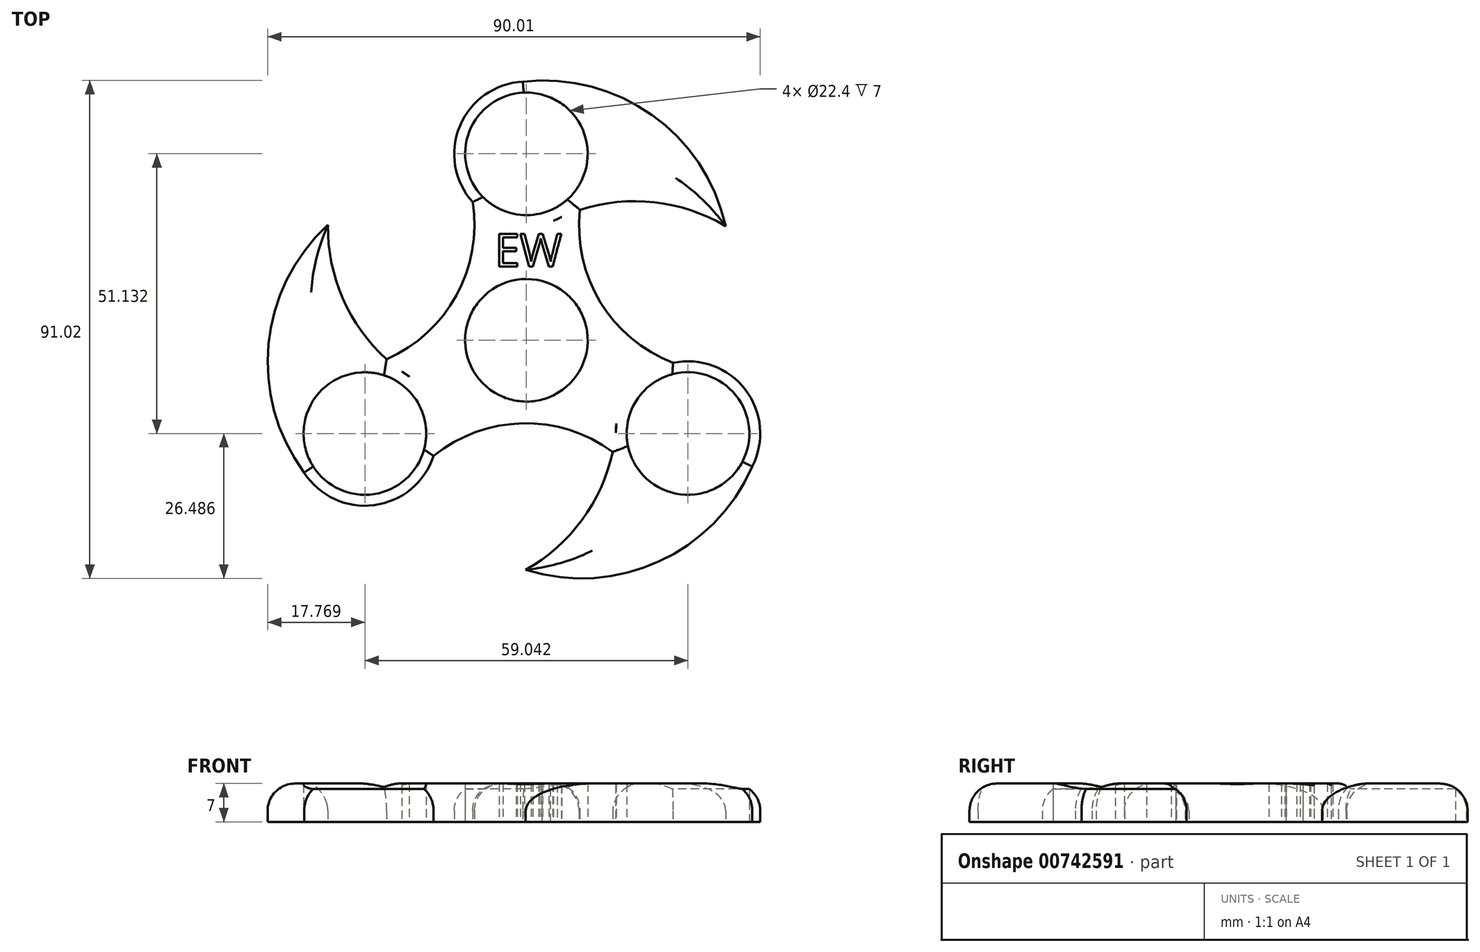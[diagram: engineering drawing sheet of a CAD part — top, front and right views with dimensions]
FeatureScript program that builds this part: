
annotation { "Feature Type Name" : "Feature", "Feature Type Description" : "" }
export const myFeature = defineFeature(function(context is Context, id is Id, definition is map)
    precondition{}
    {
        {
            var Q0;
            Q0=qCreatedBy(makeId("Top.planeOp"),FACE);
            var sketch = newSketch(context, id + "F0", { "sketchPlane" : qUnion([Q0])});
            skCircle(sketch, "E0", {"center": v(0, 0) * mm, "radius": 11.2 * mm});
            skCircle(sketch, "E1", {"center": v(0, 34.09) * mm, "radius": 11.2 * mm});
            skCircle(sketch, "E2", {"center": v(0, 34.09) * mm, "radius": 13.2 * mm});
            skCircle(sketch, "E3.1.0", {"center": v(-29.52, -17.04) * mm, "radius": 13.2 * mm});
            skCircle(sketch, "E3.1.1", {"center": v(-29.52, -17.04) * mm, "radius": 11.2 * mm});
            skCircle(sketch, "E3.2.0", {"center": v(29.52, -17.04) * mm, "radius": 13.2 * mm});
            skCircle(sketch, "E3.2.1", {"center": v(29.52, -17.04) * mm, "radius": 11.2 * mm});
            skArc(sketch, "E4", {"start": v(10.02, 25.5) * mm, "mid": v(13.1, 7.68) * mm, "end": v(26.8, -4.13) * mm});
            skArc(sketch, "E5.1.0", {"start": v(-27.09, -4.07) * mm, "mid": v(-13.2, 7.5) * mm, "end": v(-9.82, 25.27) * mm});
            skArc(sketch, "E5.2.0", {"start": v(17.07, -21.42) * mm, "mid": v(0.1, -15.18) * mm, "end": v(-16.97, -21.14) * mm});
            skArc(sketch, "E6", {"start": v(-36.28, 21.09) * mm, "mid": v(-47.14, -0.73) * mm, "end": v(-40.6, -24.2) * mm});
            skArc(sketch, "E7", {"start": v(-36.28, 21.09) * mm, "mid": v(-32.4, 5.3) * mm, "end": v(-21.4, -6.64) * mm});
            skArc(sketch, "E8.1.0", {"start": v(-0.12, -41.96) * mm, "mid": v(11.6, -30.72) * mm, "end": v(16.45, -15.21) * mm});
            skArc(sketch, "E8.1.1", {"start": v(-0.12, -41.96) * mm, "mid": v(24.2, -40.46) * mm, "end": v(41.27, -23.06) * mm});
            skArc(sketch, "E8.2.0", {"start": v(36.4, 20.87) * mm, "mid": v(20.8, 25.41) * mm, "end": v(4.95, 21.85) * mm});
            skArc(sketch, "E8.2.1", {"start": v(36.4, 20.87) * mm, "mid": v(22.94, 41.19) * mm, "end": v(-0.66, 47.27) * mm});
            skText(sketch, "E9", { "text": "EW\n", "fontName": "OpenSans-Regular.ttf"});
            const initialGuessF0  = {"E9": [-0.0058, 0.0135, 1, 0, 0.00597]};
            skSetInitialGuess(sketch, initialGuessF0);
            skSolve(sketch);
        }
        {
            var Q0;
            Q0 = qSketchRegion(id + "F0", true);
            extrude(context, id + "F1", {"entities" : qUnion([Q0]), "depth" : 7 * mm, "offsetDistance" : 25 * mm});
        }
        {
            var Q0;
            Q0=makeQuery(id+"F1.opExtrude","CAP_EDGE",EDGE,{"disambiguationData":[OSD([sQuery(id+"F0.wireOp",EDGE,"E6")])],"isStart":false});
            var Q1;
            {var subQ0=sQuery(id+"F0.wireOp",EDGE,"E3.1.0");Q1=makeQuery(id+"F1.opExtrude","CAP_EDGE",EDGE,{"disambiguationData":[OSD([subQ0]),TDD([makeQuery(id+"F0.imprint","IMPRINT",EDGE,{"disambiguationData":[TD([[makeQuery(id+"F0.imprint","INTERSECT",VERTEX,{"derivedFrom":[subQ0,sQuery(id+"F0.wireOp",EDGE,"E5.2.0")]}),1.0]])],"derivedFrom":subQ0})])],"isStart":false});}
            var Q2;
            {var subQ0=sQuery(id+"F0.wireOp",EDGE,"E7");Q2=makeQuery(id+"F1.opExtrude","CAP_EDGE",EDGE,{"disambiguationData":[OSD([subQ0]),TDD([makeQuery(id+"F0.imprint","IMPRINT",EDGE,{"disambiguationData":[TD([[makeQuery(id+"F0.imprint","INTERSECT",VERTEX,{"derivedFrom":[sQuery(id+"F0.wireOp",EDGE,"E6"),subQ0]}),-1.0]])],"derivedFrom":subQ0})])],"isStart":false});}
            var Q3;
            Q3=makeQuery(id+"F1.opExtrude","CAP_EDGE",EDGE,{"disambiguationData":[OSD([sQuery(id+"F0.wireOp",EDGE,"E5.1.0")])],"isStart":false});
            var Q4;
            Q4=makeQuery(id+"F1.opExtrude","CAP_EDGE",EDGE,{"disambiguationData":[OSD([sQuery(id+"F0.wireOp",EDGE,"E5.2.0")])],"isStart":false});
            var Q5;
            {var subQ0=sQuery(id+"F0.wireOp",EDGE,"E8.1.0");Q5=makeQuery(id+"F1.opExtrude","CAP_EDGE",EDGE,{"disambiguationData":[OSD([subQ0]),TDD([makeQuery(id+"F0.imprint","IMPRINT",EDGE,{"disambiguationData":[TD([[makeQuery(id+"F0.imprint","INTERSECT",VERTEX,{"derivedFrom":[subQ0,sQuery(id+"F0.wireOp",EDGE,"E8.1.1")]}),-1.0]])],"derivedFrom":subQ0})])],"isStart":false});}
            var Q6;
            Q6=makeQuery(id+"F1.opExtrude","CAP_EDGE",EDGE,{"disambiguationData":[OSD([sQuery(id+"F0.wireOp",EDGE,"E8.1.1")])],"isStart":false});
            var Q7;
            {var subQ0=sQuery(id+"F0.wireOp",EDGE,"E3.2.0");Q7=makeQuery(id+"F1.opExtrude","CAP_EDGE",EDGE,{"disambiguationData":[OSD([subQ0]),TDD([makeQuery(id+"F0.imprint","IMPRINT",EDGE,{"disambiguationData":[TD([[makeQuery(id+"F0.imprint","INTERSECT",VERTEX,{"derivedFrom":[subQ0,sQuery(id+"F0.wireOp",EDGE,"E4")]}),1.0]])],"derivedFrom":subQ0})])],"isStart":false});}
            var Q8;
            Q8=makeQuery(id+"F1.opExtrude","CAP_EDGE",EDGE,{"disambiguationData":[OSD([sQuery(id+"F0.wireOp",EDGE,"E4")])],"isStart":false});
            var Q9;
            {var subQ0=sQuery(id+"F0.wireOp",EDGE,"E8.2.0");Q9=makeQuery(id+"F1.opExtrude","CAP_EDGE",EDGE,{"disambiguationData":[OSD([subQ0]),TDD([makeQuery(id+"F0.imprint","IMPRINT",EDGE,{"disambiguationData":[TD([[makeQuery(id+"F0.imprint","INTERSECT",VERTEX,{"derivedFrom":[subQ0,sQuery(id+"F0.wireOp",EDGE,"E8.2.1")]}),-1.0]])],"derivedFrom":subQ0})])],"isStart":false});}
            var Q10;
            Q10=makeQuery(id+"F1.opExtrude","CAP_EDGE",EDGE,{"disambiguationData":[OSD([sQuery(id+"F0.wireOp",EDGE,"E8.2.1")])],"isStart":false});
            var Q11;
            {var subQ0=sQuery(id+"F0.wireOp",EDGE,"E2");Q11=makeQuery(id+"F1.opExtrude","CAP_EDGE",EDGE,{"disambiguationData":[OSD([subQ0]),TDD([makeQuery(id+"F0.imprint","IMPRINT",EDGE,{"disambiguationData":[TD([[makeQuery(id+"F0.imprint","INTERSECT",VERTEX,{"derivedFrom":[subQ0,sQuery(id+"F0.wireOp",EDGE,"E5.1.0")]}),1.0]])],"derivedFrom":subQ0})])],"isStart":false});}
            fillet(context, id + "F2", {"entities" : qUnion([Q0, Q1, Q2, Q3, Q4, Q5, Q6, Q7, Q8, Q9, Q10, Q11]), "radius" : 5 * mm, "tangentPropagation" : true, "allowEdgeOverflow" : false});
        }
    });
